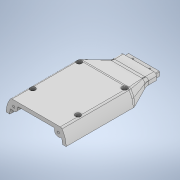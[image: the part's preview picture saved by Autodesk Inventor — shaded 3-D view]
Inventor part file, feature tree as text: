
AUTODESK INVENTOR PART (.ipt)
format: ipt  version: 2021 (Build 250183000, 183)  size: 2,152,448 bytes
history: native  units: mm
features: fillet x13, sketch x9, extrude x8, plane x3, other x2, loft x1, mirror x1, delete_face x1, hole x1
ambient origin geometry x8: Origin, YZ Plane, XZ Plane, XY Plane, X Axis, Y Axis, Z Axis, Center Point
bodies: Body1 (feature_tree)
feature tree (39):
  extrude  "Extrusion2"  Depth=7.0mm
  extrude  "Extrusion3"  Depth=68.0mm
  fillet  "Rundung4"  Radius=12.0mm
  plane  "Arbeitsebene3"
  fillet  "Rundung5"  Radius=34.0mm
  plane  "Arbeitsebene4"
  extrude  "Extrusion4"  Depth=30.0mm TaperAngle=0.0deg
  loft  "Erhebung5"
  plane  "Arbeitsebene5"
  sketch  "Skizze18"  dims[d42=4.0mm d43=4.0mm]
  extrude  "Extrusion14"  Depth=10.0mm TaperAngle=0.0deg
  mirror  "Spiegeln3"
  delete_face  "Fläche löschen4"
  hole  "Bohrung3"  [1 undecoded]
  fillet  "Rundung23"  Radius=57.0mm
  fillet  "Rundung24"  Radius=50.0mm
  fillet  "Rundung25"  Radius=130.0mm
  fillet  "Rundung26"  [1 undecoded]
  fillet  "Rundung27"  Radius=80.0mm
  fillet  "Rundung28"  Radius=13.0mm
  fillet  "Rundung29"  Radius=43.0mm
  fillet  "Rundung30"  Radius=13.0mm
  extrude  "Extrusion21"  Depth=10.0mm
  extrude  "Extrusion22"  TaperAngle=0.0deg  [1 undecoded]
  fillet  "Rundung31"  [1 undecoded]
  fillet  "Rundung32"  [1 undecoded]
  fillet  "Rundung33"  [1 undecoded]
  extrude  "Extrusion23"  TaperAngle=0.0deg  [1 undecoded]
  extrude  "Extrusion24"  TaperAngle=0.0deg  [1 undecoded]
  sketch  "Skizze10"  dims[d33=7.0mm d34=7.0mm]
  sketch  "Skizze11"  dims[d35=7.0mm d36=68.0mm d37=12.0mm d38=34.0mm]
  sketch  "Skizze16"  dims[d39=0.0mm d40=30.0mm d41=0.0mm]
  sketch  "Skizze29"  dims[d44=4.0mm d45=10.0mm d46=0.0mm]
  other  "Kanten7"
  other  "Kanten8"
  sketch  "Skizze39"  dims[d49=1.0mm d50=60.0mm d62=5.0mm]
  sketch  "Skizze41"  dims[d70=35.0mm d72=7.0mm d82=75.0mm d84=57.0mm d85=7.0mm d87=50.0mm d88=130.0mm d89=0.0mm d92=0.0mm d93=90.0deg d128=80.0mm d129=13.0mm d130=43.0mm]
  sketch  "Skizze42"  dims[d133=12.15mm d152=10.0mm d153=91.5mm d189=65.0mm d190=0.0mm d191=13.0mm]
  sketch  "Skizze43"  dims[d192=43.0mm d193=168.5mm d194=5.5mm d195=6.0mm d196=4.0mm d197=2.0mm d198=90.0deg d199=62.05mm d200=0.0mm d201=0.0mm d202=0.0mm d203=0.0mm d204=0.0mm d205=0.0mm d206=0.0mm d207=0.0mm d208=0.0mm d212=101.5mm d265=20.0mm d267=7.0mm d270=7.0mm d271=7.0mm d287=0.0mm d288=90.0deg d289=50.0mm d290=50.0mm d317=10.0mm d318=10.0mm d319=4.0mm d320=10.0mm d321=20.0mm d322=2.0mm d323=3.0mm d324=2.0mm d325=2.4mm d326=16.2mm d327=5.0mm d328=14.25mm d329=0.0mm d332=15.0mm d333=42.4mm d334=16.0mm d335=20.0mm d336=0.0mm d337=2.0mm d338=2.0mm d339=1.5mm d340=4.2mm d341=4.2mm d342=15.0mm d343=0.0mm d344=10.0mm d345=6.0mm d346=0.0mm d347=10.0mm d348=10.0mm d349=10.0mm d248=0.5mm d249=0.872665mm d250=0.5mm d251=0.872665mm]
note: 8 required parameter values undecoded (feature->parameter linkage not recoverable at this tier; creation-order binding heuristic only, values carry confidence <= 0.55)
